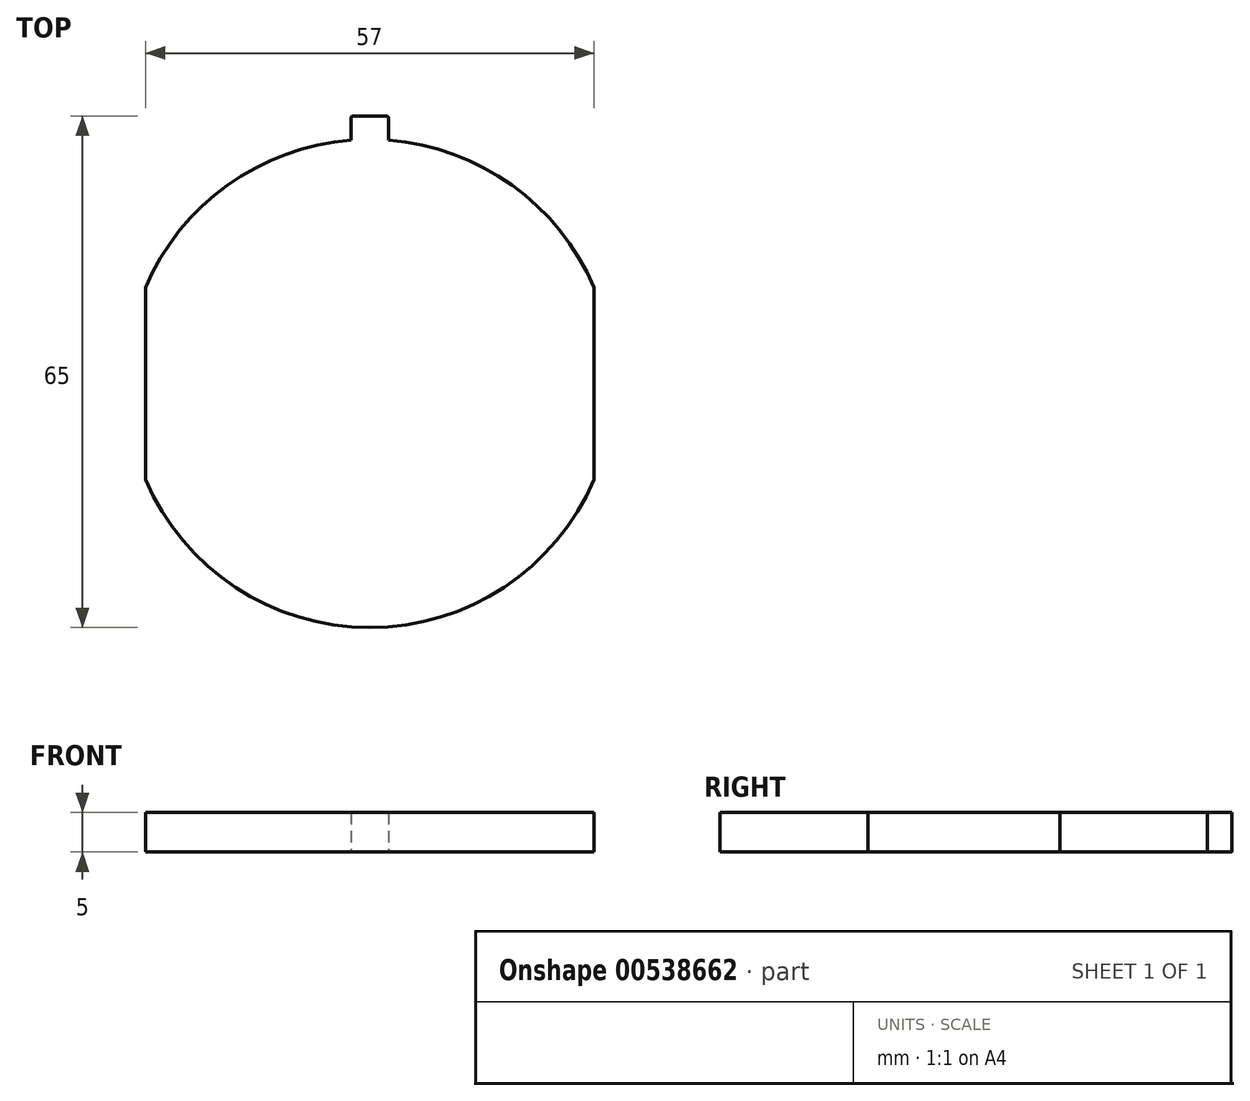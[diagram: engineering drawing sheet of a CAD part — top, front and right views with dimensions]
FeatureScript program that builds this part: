
annotation { "Feature Type Name" : "Feature", "Feature Type Description" : "" }
export const myFeature = defineFeature(function(context is Context, id is Id, definition is map)
    precondition{}
    {
        {
            var Q0;
            Q0=qCreatedBy(makeId("Top.planeOp"),FACE);
            var sketch = newSketch(context, id + "F0", { "sketchPlane" : qUnion([Q0])});
            skArc(sketch, "E0", {"start": v(-2.38, 30.9) * mm, "mid": v(-18.05, 25.2) * mm, "end": v(-28.5, 12.2) * mm});
            skLineSegment(sketch, "E1.bottom", {"start": v(2.38, 30.9) * mm, "end": v(2.38, 30.9) * mm});
            skLineSegment(sketch, "E1.top", {"start": v(-2.13, 34) * mm, "end": v(2.13, 34) * mm});
            skLineSegment(sketch, "E1.left", {"start": v(-2.38, 30.9) * mm, "end": v(-2.38, 33.75) * mm});
            skLineSegment(sketch, "E1.right", {"start": v(2.38, 30.9) * mm, "end": v(2.38, 33.75) * mm});
            skPoint(sketch, "E2", {"position": v(0, 34) * mm});
            skPoint(sketch, "E3.visualSharp", {"position": v(-2.38, 34) * mm});
            skArc(sketch, "E3.filletArc", {"start": v(-2.13, 34) * mm, "mid": v(-2.3, 33.93) * mm, "end": v(-2.38, 33.75) * mm});
            skPoint(sketch, "E4.visualSharp", {"position": v(2.38, 34) * mm});
            skArc(sketch, "E4.filletArc", {"start": v(2.38, 33.75) * mm, "mid": v(2.3, 33.93) * mm, "end": v(2.13, 34) * mm});
            skLineSegment(sketch, "E5", {"start": v(-28.5, 12.2) * mm, "end": v(-28.5, -12.2) * mm});
            skLineSegment(sketch, "E6", {"start": v(28.5, 12.2) * mm, "end": v(28.5, -12.2) * mm});
            skArc(sketch, "E7", {"start": v(-28.5, 12.2) * mm, "mid": v(-31, 0) * mm, "end": v(-28.5, -12.2) * mm, "construction": true});
            skArc(sketch, "E8", {"start": v(-28.5, -12.2) * mm, "mid": v(0, -31) * mm, "end": v(28.5, -12.2) * mm});
            skArc(sketch, "E9", {"start": v(28.5, 12.2) * mm, "mid": v(18.05, 25.2) * mm, "end": v(2.38, 30.9) * mm});
            skArc(sketch, "E10", {"start": v(28.5, -12.2) * mm, "mid": v(31, 0) * mm, "end": v(28.5, 12.2) * mm, "construction": true});
            skSolve(sketch);
        }
        {
            var Q0;
            Q0 = qSketchRegion(id + "F0", true);
            extrude(context, id + "F1", {"entities" : qUnion([Q0]), "depth" : 5 * mm, "offsetDistance" : 25 * mm});
        }
    });
